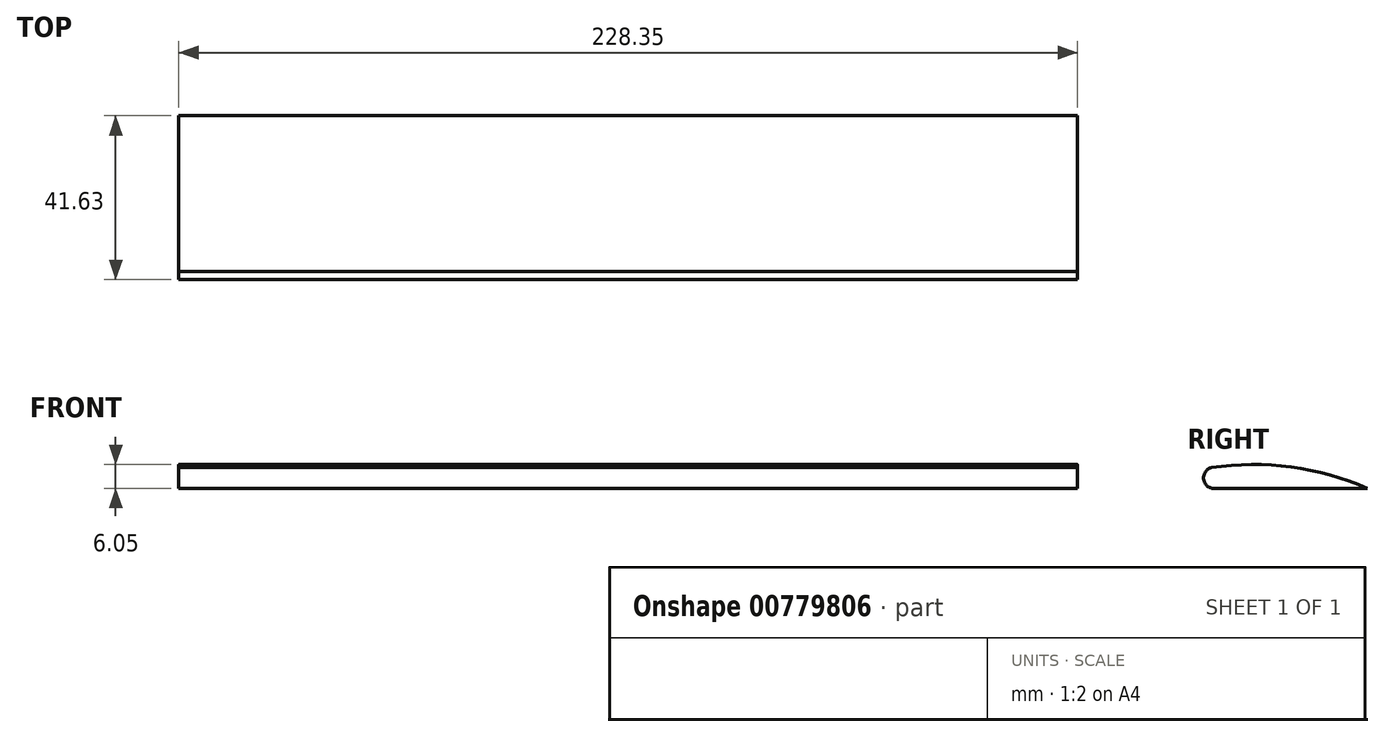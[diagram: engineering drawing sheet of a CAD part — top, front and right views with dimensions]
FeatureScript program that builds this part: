
annotation { "Feature Type Name" : "Feature", "Feature Type Description" : "" }
export const myFeature = defineFeature(function(context is Context, id is Id, definition is map)
    precondition{}
    {
        {
            var Q0;
            Q0=qCreatedBy(makeId("Right.planeOp"),FACE);
            var sketch = newSketch(context, id + "F0", { "sketchPlane" : qUnion([Q0])});
            skArc(sketch, "E0", {"start": v(0, 5.26) * mm, "mid": v(-2.03, 2.63) * mm, "end": v(0, 0) * mm});
            skArc(sketch, "E1", {"start": v(39.6, 0) * mm, "mid": v(20.17, 5.42) * mm, "end": v(0, 5.26) * mm});
            skLineSegment(sketch, "E2", {"start": v(0, 0) * mm, "end": v(39.6, 0) * mm});
            skSolve(sketch);
        }
        {
            var Q0;
            Q0 = qSketchRegion(id + "F0", true);
            extrude(context, id + "F1", {"entities" : qUnion([Q0]), "depth" : 228.35 * mm, "offsetDistance" : 25.4 * mm});
        }
    });
